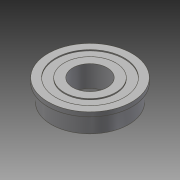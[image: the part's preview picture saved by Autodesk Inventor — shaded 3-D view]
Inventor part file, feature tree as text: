
AUTODESK INVENTOR PART (.ipt)
format: ipt  version: 2014 SP1 (Build 180222100, 222)  size: 107,520 bytes
history: native  units: in
note: dims shown in document units (in); Inventor stores cm internally (conversion verified against a paired STEP export)
features: revolve x1, other x1, imported_body x1
ambient origin geometry x8: Origin, YZ Plane, XZ Plane, XY Plane, X Axis, Y Axis, Z Axis, Center Point
bodies: Body1 (feature_tree)
feature tree (3):
  revolve  "Revolve1"  [1 undecoded]
  other  "217-2731.ipt1"
  imported_body  "Base1"
note: 1 required parameter value undecoded (feature->parameter linkage not recoverable at this tier; creation-order binding heuristic only, values carry confidence <= 0.55)
